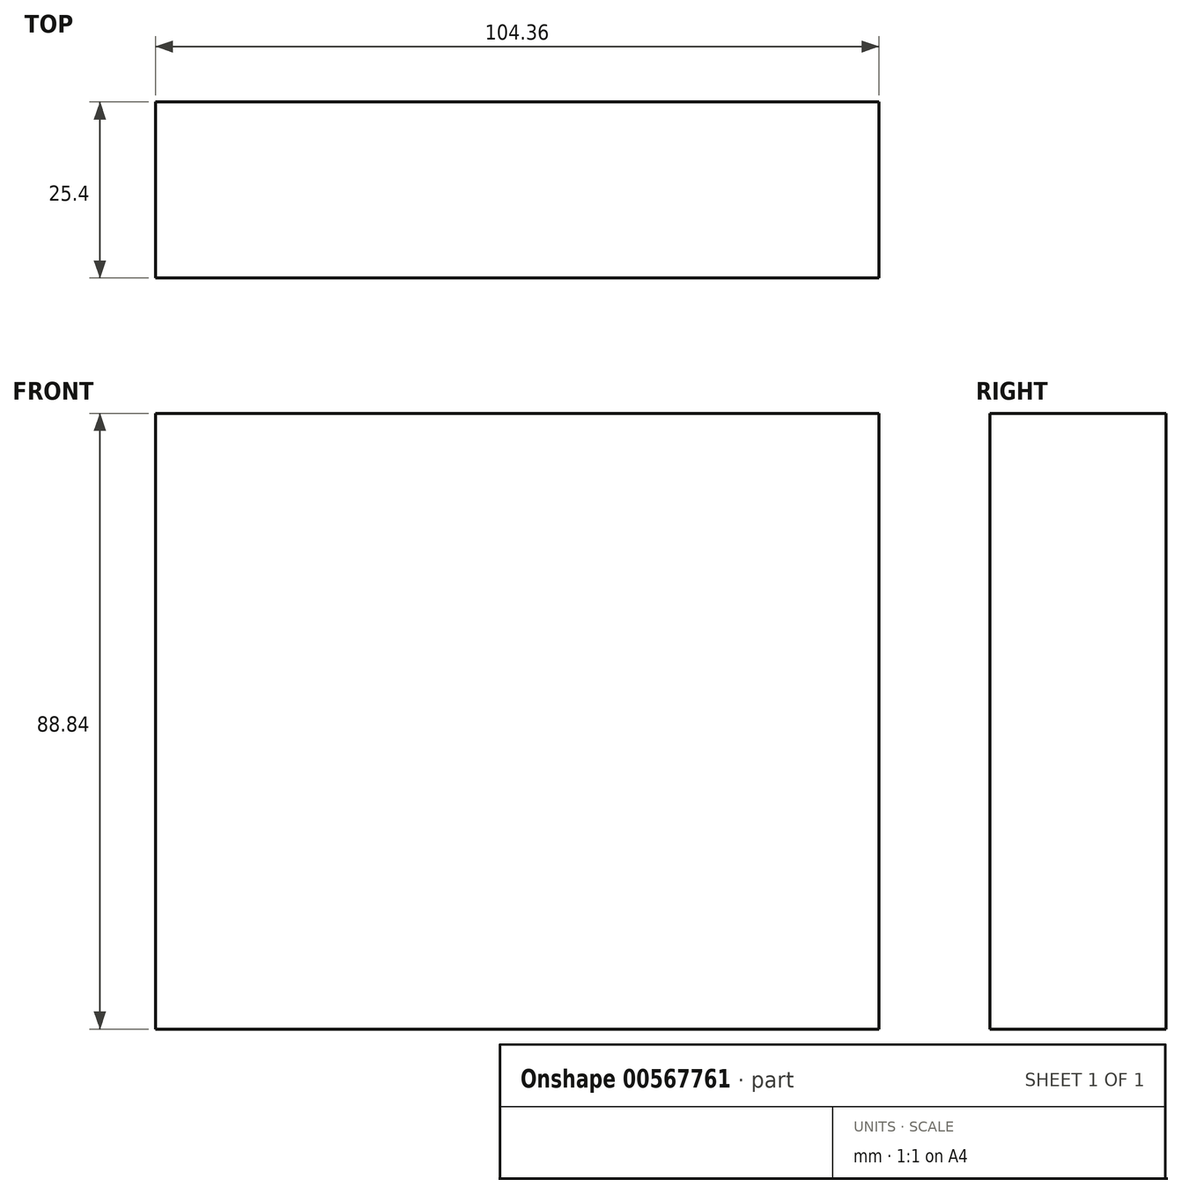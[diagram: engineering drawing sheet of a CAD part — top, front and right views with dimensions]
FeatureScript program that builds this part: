
annotation { "Feature Type Name" : "Feature", "Feature Type Description" : "" }
export const myFeature = defineFeature(function(context is Context, id is Id, definition is map)
    precondition{}
    {
        {
            var Q0;
            Q0=qCreatedBy(makeId("Front.planeOp"),FACE);
            var sketch = newSketch(context, id + "F0", { "sketchPlane" : qUnion([Q0])});
            skLineSegment(sketch, "E0.bottom", {"start": v(-50.18, 44.6) * mm, "end": v(54.18, 44.6) * mm});
            skLineSegment(sketch, "E0.top", {"start": v(-50.18, -44.24) * mm, "end": v(54.18, -44.24) * mm});
            skLineSegment(sketch, "E0.left", {"start": v(-50.18, 44.6) * mm, "end": v(-50.18, -44.24) * mm});
            skLineSegment(sketch, "E0.right", {"start": v(54.18, 44.6) * mm, "end": v(54.18, -44.24) * mm});
            skSolve(sketch);
        }
        {
            var Q0;
            Q0=sQuery(id+"F0.wireOp",EDGE,"E0.bottom");
            var Q1;
            Q1=sQuery(id+"F0.wireOp",EDGE,"E0.right");
            var Q2;
            Q2=sQuery(id+"F0.wireOp",EDGE,"E0.top");
            var Q3;
            Q3=sQuery(id+"F0.wireOp",EDGE,"E0.left");
            extrude(context, id + "F1", {"bodyType" : ToolBodyType.SURFACE, "surfaceEntities" : qUnion([Q0, Q1, Q2, Q3]), "oppositeDirection" : true, "depth" : 25.4 * mm, "offsetDistance" : 25.4 * mm});
        }
    });
